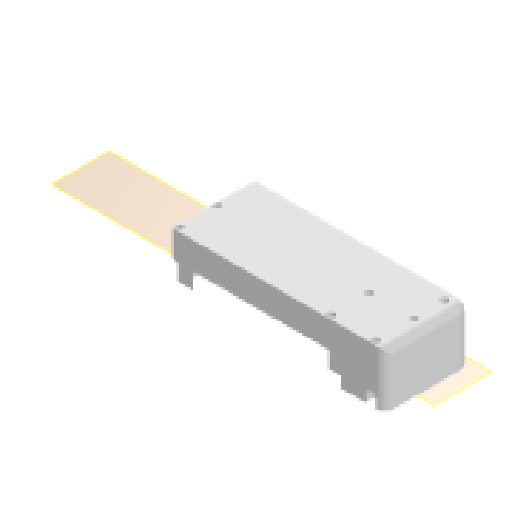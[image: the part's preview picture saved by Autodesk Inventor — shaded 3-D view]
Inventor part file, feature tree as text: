
AUTODESK INVENTOR PART (.ipt)
format: ipt  version: 2025.3 (Build 293356000, 356)  size: 226,304 bytes
history: native  units: mm
features: sketch x5, reference x5, other x5, extrude x4, projected_geometry x2, plane x1, fillet x1, hole x1
ambient origin geometry x8: Origin, YZ Plane, XZ Plane, XY Plane, X Axis, Y Axis, Z Axis, Center Point
bodies: Volumenkörper1 (feature_tree)
feature tree (24):
  plane  "Arbeitsebene1"
  extrude  "Extrusion1"  TaperAngle=0.0deg  [1 undecoded]
  fillet  "Rundung1"  Radius=32.0mm
  hole  "Bohrung1"  [1 undecoded]
  extrude  "Extrusion2"  Depth=10.0mm TaperAngle=0.0deg
  extrude  "Extrusion3"  Depth=18.0mm
  extrude  "Extrusion4"  Depth=4.0mm TaperAngle=0.0deg
  sketch  "Skizze1"  dims[d0=80.0mm d1=0.0mm d2=32.0mm]
  reference  "Referenz1"
  reference  "Referenz2"
  reference  "Referenz3"
  sketch  "Skizze2"  dims[d3=20.0mm d4=0.0mm d5=3.0mm]
  projected_geometry  "Projizierte Kontur1"
  sketch  "Skizze3"  dims[d6=3.5mm d7=6.0mm d8=4.0mm d9=2.0mm d10=90.0deg d11=10.0mm d12=20.594885mm d13=18.0mm d14=0.0mm]
  projected_geometry  "Projizierte Kontur2"
  sketch  "Skizze4"  dims[d15=27.0mm d16=18.0mm]
  reference  "Referenz4"
  sketch  "Sketch5"  dims[d17=18.0mm d18=0.0mm d19=4.0mm d20=0.0mm]
  reference  "Reference5"
  other  "<userpath>\Documents\HoLiSheet\INVENTOR\Assembly_HoliSheet_v6.iam"
  other  "Assembly_HoliSheet_v6.iam"
  other  "10_Wellplate_base_v6:1"
  other  "Assemlby_lightsheet_generator_passive_v2:1"
  other  "30_Lightsheet_generator_singlegalvo:1"
note: 2 required parameter values undecoded (feature->parameter linkage not recoverable at this tier; creation-order binding heuristic only, values carry confidence <= 0.55)
